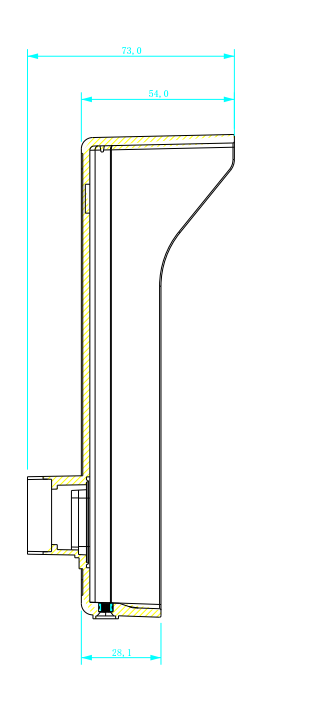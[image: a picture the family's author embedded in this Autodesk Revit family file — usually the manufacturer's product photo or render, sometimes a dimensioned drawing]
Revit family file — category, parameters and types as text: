
# Revit family: SH-47T
name_source: partatom
category: Устройства связи
units: mm (PartAtom-declared; Revit-internal decimal feet)

## family parameters
Всегда вертикально = Нет
На основе рабочей плоскости = Да
Общий = Да
При загрузке вырезать с полостями = Нет
Размер круглого соединителя = Использовать диаметр
Сохранять ориентацию аннотаций = Нет
Тип детали = Нормальный
Точка принадлежности помещению = Нет

## types (1)
- SH-47T
    ADSK_URL документации изделия = http://cdn.bas-ip.com
    ADSK_URL страницы изделия = https://www.bas-ip.ru
    ADSK_Версия Revit = Revit 2020
    ADSK_Единица измерения = шт
    ADSK_Завод-изготовитель = BAS-IP
    ADSK_Классификация нагрузок = Кнопка универсальная бесконтактная
    ADSK_Количество фаз = 1
    ADSK_Коэффициент мощности = 0.9
    ADSK_Марка = SH-47T
    ADSK_Наименование = Кнопка универсальная бесконтактная SH-47T
    ADSK_Наименование краткое = SH-47T
    ADSK_Напряжение = 12 В
    ADSK_Номинальная мощность = 1 Вт
    ADSK_Полная мощность = 1 В·А
    ADSK_Размер_Длина = 86 мм
    ADSK_Размер_Толщина = 20 мм
    ADSK_Размер_Ширина = 86 мм
    BIM library = https://bimlib.ru
    URL = https://www.bas-ip.ru
    Группа модели = Кнопка универсальная бесконтактная SH-47T
    Дополнительно = • Возможность изменения (переключения) цвета подсветки
• Триггерный режим
• Пластина из алюминия
    Допустимая влажность = 10% – 94%
    Изготовитель = BAS-IP
    Изображение типоразмера = <Нет>
    Материал корпуса = Матеріал светло-серый
    Напряжение питания = +12В (+1%, - 15%)
    Описание = BAS-IP SH-47T – бесконтактная кнопка для подключения к индивидуальной или многоабонентской вызывной панели. Данная кнопка имеет квадратный форм-фактор и может использоваться как дополнительная бесконтактная кнопка, которая дублирует кнопку вызова абонента или консьержа в вызывных панелях. Рекомендуется устанавливать на расстоянии опущенной руки.
    Отметка по умолчанию = 0 мм
    Размеры = 86×86×19,5 мм
    Ресурс работы = Более 100 миллионов нажатий
    Степень защиты = IP68
    Температурный режим = -27 – +60 °C
    Тип кнопки = Бесконтактная
    Цвет = Черный, серебро
